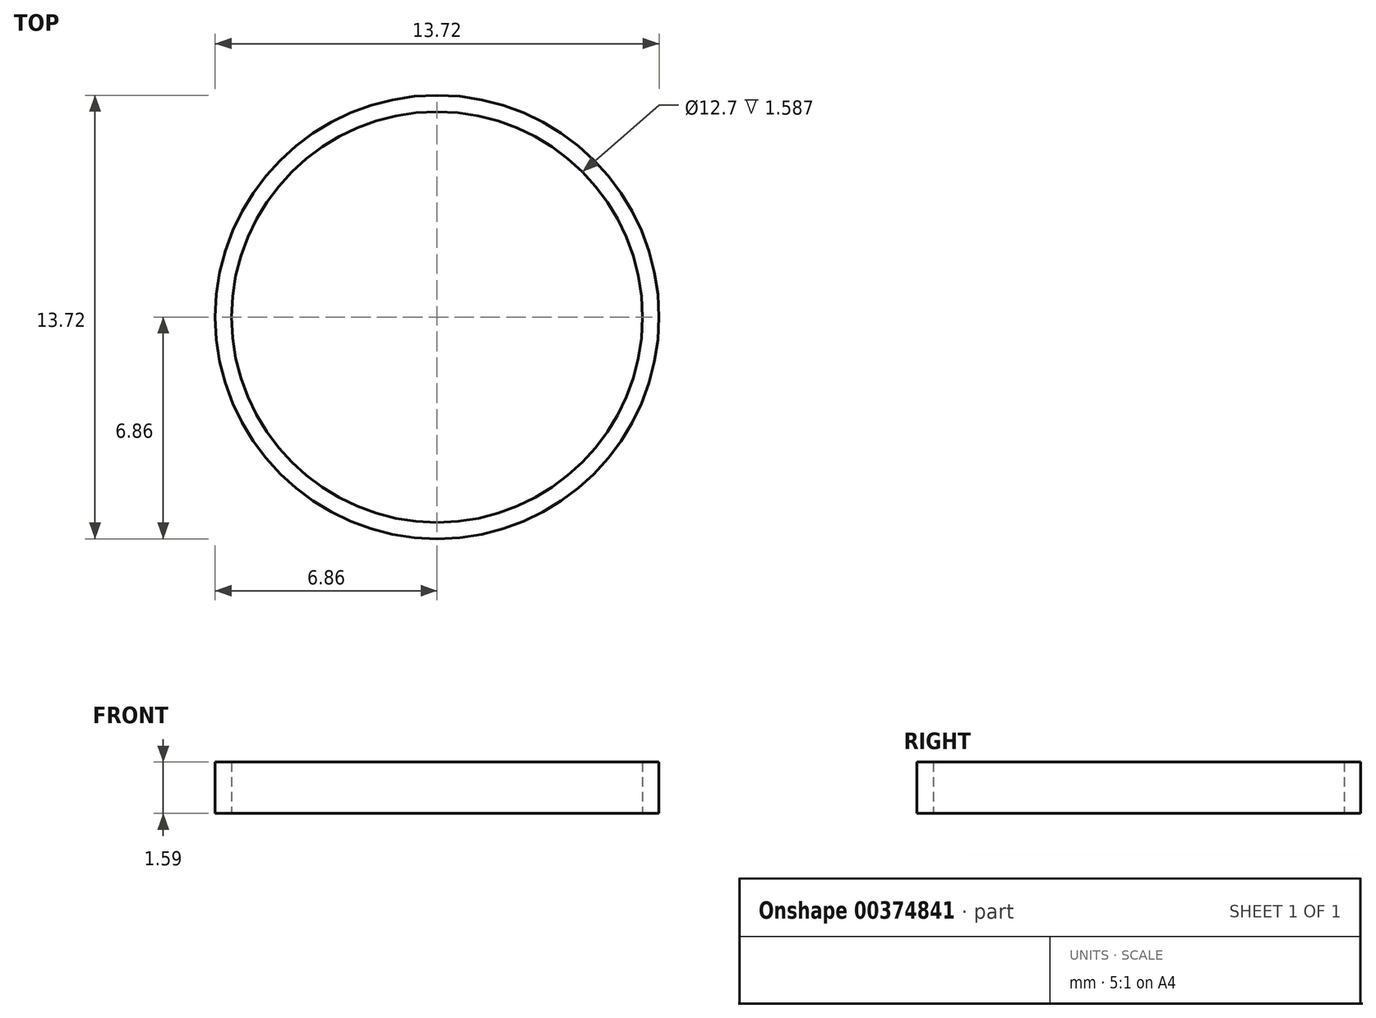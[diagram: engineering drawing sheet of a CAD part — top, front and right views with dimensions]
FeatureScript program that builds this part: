
annotation { "Feature Type Name" : "Feature", "Feature Type Description" : "" }
export const myFeature = defineFeature(function(context is Context, id is Id, definition is map)
    precondition{}
    {
        {
            var Q0;
            Q0=qCreatedBy(makeId("Top.planeOp"),FACE);
            var sketch = newSketch(context, id + "F0", { "sketchPlane" : qUnion([Q0])});
            skCircle(sketch, "E0", {"center": v(0, 0) * mm, "radius": 6.86 * mm});
            skCircle(sketch, "E1", {"center": v(0, 0) * mm, "radius": 6.35 * mm});
            skSolve(sketch);
        }
        {
            var Q0;
            Q0=makeQuery(id+"F0.imprint","IMPRINT",FACE,{"disambiguationData":[TD([[makeQuery(id+"F0.imprint","IMPRINT",EDGE,{"derivedFrom":sQuery(id+"F0.wireOp",EDGE,"E0")}),1.0]])]});
            extrude(context, id + "F1", {"entities" : qUnion([Q0]), "depth" : 1.59 * mm});
        }
    });
